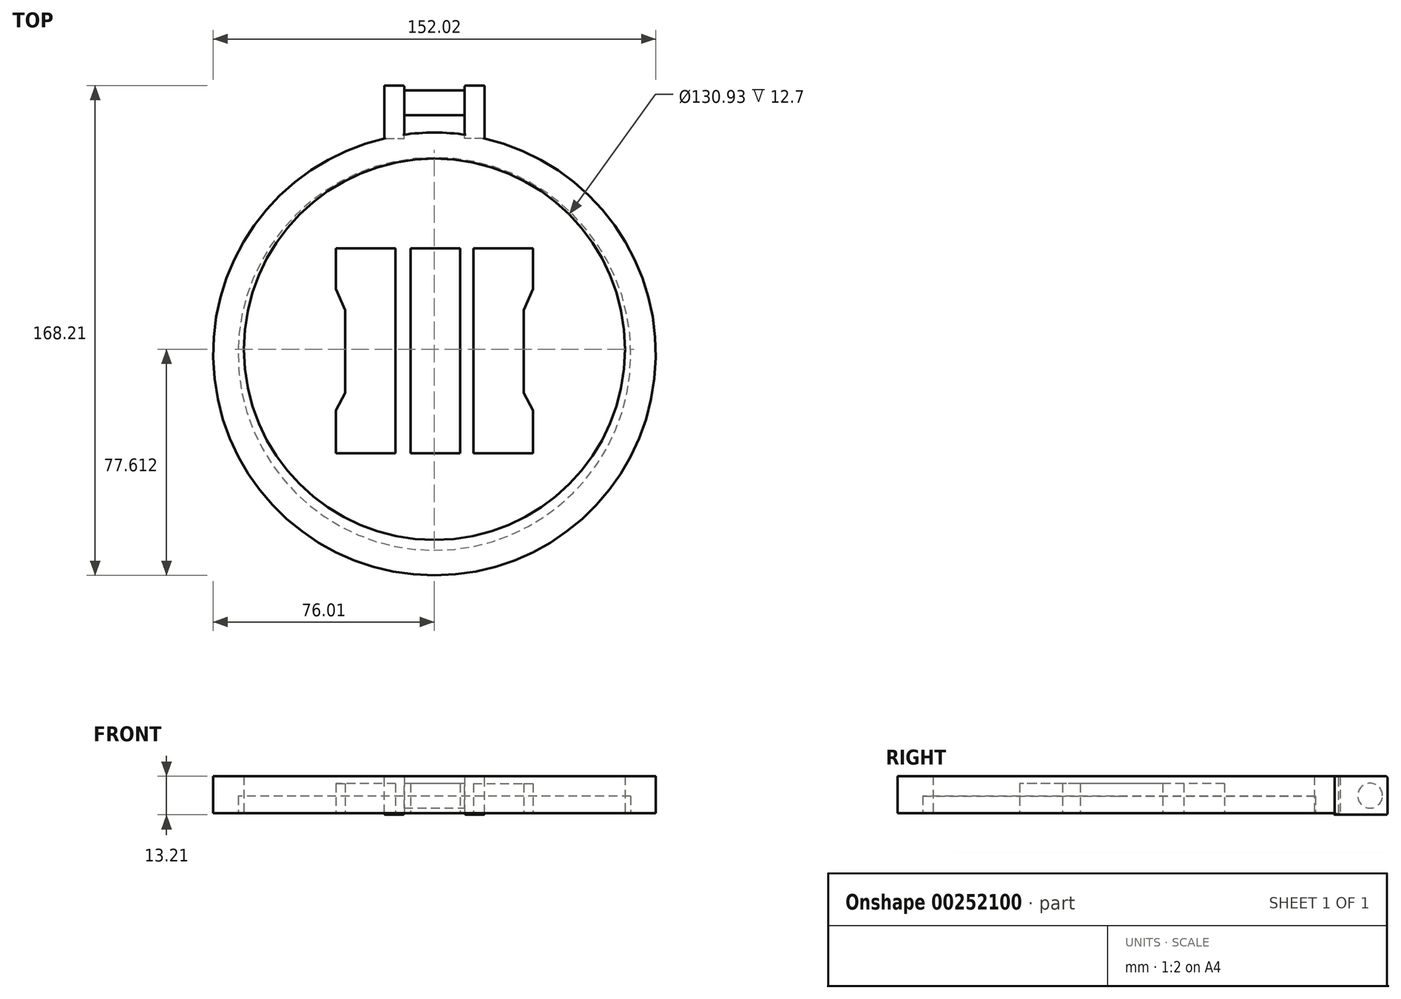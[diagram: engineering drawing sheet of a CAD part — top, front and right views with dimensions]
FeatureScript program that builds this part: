
annotation { "Feature Type Name" : "Feature", "Feature Type Description" : "" }
export const myFeature = defineFeature(function(context is Context, id is Id, definition is map)
    precondition{}
    {
        {
            var Q0;
            Q0=qCreatedBy(makeId("Top.planeOp"),FACE);
            var sketch = newSketch(context, id + "F0", { "sketchPlane" : qUnion([Q0])});
            skLineSegment(sketch, "E0", {"start": v(-13.34, 36.21) * mm, "end": v(-13.34, -34.08) * mm});
            skLineSegment(sketch, "E1", {"start": v(-13.34, 36.21) * mm, "end": v(-33.85, 36.21) * mm});
            skLineSegment(sketch, "E2", {"start": v(-33.85, 36.21) * mm, "end": v(-33.85, 22.33) * mm});
            skLineSegment(sketch, "E3", {"start": v(-33.85, 22.33) * mm, "end": v(-30.65, 15.06) * mm});
            skLineSegment(sketch, "E4", {"start": v(-30.65, 15.06) * mm, "end": v(-30.65, -13.35) * mm});
            skLineSegment(sketch, "E5", {"start": v(-30.65, -13.35) * mm, "end": v(-33.85, -19.33) * mm});
            skLineSegment(sketch, "E6", {"start": v(-33.85, -19.33) * mm, "end": v(-33.85, -34.08) * mm});
            skLineSegment(sketch, "E7", {"start": v(-33.85, -34.08) * mm, "end": v(-13.34, -34.08) * mm});
            skLineSegment(sketch, "E8", {"start": v(-8.21, 36.21) * mm, "end": v(-8.21, -34.08) * mm});
            skLineSegment(sketch, "E9", {"start": v(-8.21, -34.08) * mm, "end": v(8.88, -34.08) * mm});
            skLineSegment(sketch, "E10", {"start": v(8.88, -34.08) * mm, "end": v(8.88, 36.21) * mm});
            skLineSegment(sketch, "E11", {"start": v(8.88, 36.21) * mm, "end": v(-8.21, 36.21) * mm});
            skLineSegment(sketch, "E12.MirrorCS", {"start": v(13.34, 36.21) * mm, "end": v(33.85, 36.21) * mm});
            skLineSegment(sketch, "E13.MirrorCS", {"start": v(13.34, 36.21) * mm, "end": v(13.34, -34.08) * mm});
            skLineSegment(sketch, "E14.MirrorCS", {"start": v(33.85, 36.21) * mm, "end": v(33.85, 22.33) * mm});
            skLineSegment(sketch, "E15.MirrorCS", {"start": v(33.85, 22.33) * mm, "end": v(30.65, 15.06) * mm});
            skLineSegment(sketch, "E16.MirrorCS", {"start": v(30.65, 15.06) * mm, "end": v(30.65, -13.35) * mm});
            skLineSegment(sketch, "E17.MirrorCS", {"start": v(30.65, -13.35) * mm, "end": v(33.85, -19.33) * mm});
            skLineSegment(sketch, "E18.MirrorCS", {"start": v(33.85, -34.08) * mm, "end": v(13.34, -34.08) * mm});
            skLineSegment(sketch, "E19.MirrorCS", {"start": v(33.85, -19.33) * mm, "end": v(33.85, -34.08) * mm});
            skCircle(sketch, "E20", {"center": v(0, 0) * mm, "radius": 76.01 * mm});
            skCircle(sketch, "E21", {"center": v(0, 1.6) * mm, "radius": 65.46 * mm});
            skSolve(sketch);
        }
        {
            var Q0;
            Q0=makeQuery(id+"F0.imprint","IMPRINT",FACE,{"disambiguationData":[TD([[makeQuery(id+"F0.imprint","IMPRINT",EDGE,{"derivedFrom":sQuery(id+"F0.wireOp",EDGE,"E20")}),1.0]])]});
            extrude(context, id + "F1", {"entities" : qUnion([Q0]), "depth" : 12.7 * mm});
        }
        {
            var Q0;
            Q0=makeQuery(id+"F0.imprint","IMPRINT",FACE,{"disambiguationData":[TD([[makeQuery(id+"F0.imprint","IMPRINT",EDGE,{"derivedFrom":sQuery(id+"F0.wireOp",EDGE,"E0")}),-1.0]])]});
            var Q1;
            Q1=makeQuery(id+"F0.imprint","IMPRINT",FACE,{"disambiguationData":[TD([[makeQuery(id+"F0.imprint","IMPRINT",EDGE,{"derivedFrom":sQuery(id+"F0.wireOp",EDGE,"E8")}),1.0]])]});
            var Q2;
            Q2=makeQuery(id+"F0.imprint","IMPRINT",FACE,{"disambiguationData":[TD([[makeQuery(id+"F0.imprint","IMPRINT",EDGE,{"derivedFrom":sQuery(id+"F0.wireOp",EDGE,"E12.MirrorCS")}),-1.0]])]});
            extrude(context, id + "F2", {"entities" : qUnion([Q0, Q1, Q2]), "depth" : 10.16 * mm});
        }
        {
            var Q0;
            Q0=qCreatedBy(makeId("Top.planeOp"),FACE);
            var sketch = newSketch(context, id + "F3", { "sketchPlane" : qUnion([Q0])});
            skCircle(sketch, "E22", {"center": v(0, 0) * mm, "radius": 67.42 * mm});
            skSolve(sketch);
        }
        {
            var Q0;
            Q0 = qSketchRegion(id + "F3", true);
            extrude(context, id + "F4", {"entities" : qUnion([Q0]), "depth" : 5.84 * mm});
        }
        {
            var Q0;
            Q0=makeQuery(id+"F1.opExtrude","CAP_FACE",FACE,{"disambiguationData":[OSD([sQuery(id+"F0.wireOp",EDGE,"E20"),sQuery(id+"F0.wireOp",EDGE,"E21")])],"isStart":false});
            var sketch = newSketch(context, id + "F5", { "sketchPlane" : qUnion([Q0])});
            skLineSegment(sketch, "E23.bottom", {"start": v(-17.26, 74.03) * mm, "end": v(-10.36, 74.03) * mm});
            skLineSegment(sketch, "E23.top", {"start": v(-17.26, 92.2) * mm, "end": v(-10.36, 92.2) * mm});
            skLineSegment(sketch, "E23.left", {"start": v(-17.26, 74.03) * mm, "end": v(-17.26, 92.2) * mm});
            skLineSegment(sketch, "E23.right", {"start": v(-10.36, 74.03) * mm, "end": v(-10.36, 92.2) * mm});
            skLineSegment(sketch, "E24.MirrorCS", {"start": v(10.36, 74.03) * mm, "end": v(10.36, 92.2) * mm});
            skLineSegment(sketch, "E25.MirrorCS", {"start": v(17.26, 74.03) * mm, "end": v(10.36, 74.03) * mm});
            skLineSegment(sketch, "E26.MirrorCS", {"start": v(17.26, 74.03) * mm, "end": v(17.26, 92.2) * mm});
            skLineSegment(sketch, "E27.MirrorCS", {"start": v(17.26, 92.2) * mm, "end": v(10.36, 92.2) * mm});
            skSolve(sketch);
        }
        {
            var Q0;
            Q0 = qSketchRegion(id + "F5", true);
            extrude(context, id + "F6", {"entities" : qUnion([Q0]), "operationType" : NewBodyOperationType.ADD, "oppositeDirection" : true, "depth" : 13.2 * mm});
        }
        {
            var Q0;
            Q0=makeQuery(id+"F6.opExtrude","CAP_EDGE",EDGE,{"disambiguationData":[OSD([sQuery(id+"F5.wireOp",EDGE,"E23.top")])],"isStart":true});
            var Q1;
            Q1=makeQuery(id+"F6.opExtrude","CAP_EDGE",EDGE,{"disambiguationData":[OSD([sQuery(id+"F5.wireOp",EDGE,"E27.MirrorCS")])],"isStart":true});
            var Q2;
            Q2=makeQuery(id+"F6.opExtrude","CAP_EDGE",EDGE,{"disambiguationData":[OSD([sQuery(id+"F5.wireOp",EDGE,"E24.MirrorCS")])],"isStart":true});
            var Q3;
            Q3=makeQuery(id+"F6.opExtrude","CAP_EDGE",EDGE,{"disambiguationData":[OSD([sQuery(id+"F5.wireOp",EDGE,"E26.MirrorCS")])],"isStart":true});
            var Q4;
            Q4=makeQuery(id+"F6.opExtrude","SWEPT_EDGE",EDGE,{"disambiguationData":[OSD([sQuery(id+"F5.wireOp",EDGE,"E26.MirrorCS"),sQuery(id+"F5.wireOp",EDGE,"E27.MirrorCS")])]});
            var Q5;
            Q5=makeQuery(id+"F6.opExtrude","CAP_EDGE",EDGE,{"disambiguationData":[OSD([sQuery(id+"F5.wireOp",EDGE,"E27.MirrorCS")])],"isStart":false});
            var Q6;
            Q6=makeQuery(id+"F6.opExtrude","SWEPT_EDGE",EDGE,{"disambiguationData":[OSD([sQuery(id+"F5.wireOp",EDGE,"E24.MirrorCS"),sQuery(id+"F5.wireOp",EDGE,"E27.MirrorCS")])]});
            var Q7;
            Q7=makeQuery(id+"F6.opExtrude","SWEPT_EDGE",EDGE,{"disambiguationData":[OSD([sQuery(id+"F5.wireOp",EDGE,"E23.top"),sQuery(id+"F5.wireOp",EDGE,"E23.left")])]});
            var Q8;
            Q8=makeQuery(id+"F6.opExtrude","CAP_EDGE",EDGE,{"disambiguationData":[OSD([sQuery(id+"F5.wireOp",EDGE,"E23.top")])],"isStart":false});
            var Q9;
            Q9=makeQuery(id+"F6.opExtrude","SWEPT_EDGE",EDGE,{"disambiguationData":[OSD([sQuery(id+"F5.wireOp",EDGE,"E23.top"),sQuery(id+"F5.wireOp",EDGE,"E23.right")])]});
            var Q10;
            Q10=makeQuery(id+"F6.opExtrude","CAP_EDGE",EDGE,{"disambiguationData":[OSD([sQuery(id+"F5.wireOp",EDGE,"E24.MirrorCS")])],"isStart":false});
            var Q11;
            Q11=makeQuery(id+"F6.opExtrude","CAP_EDGE",EDGE,{"disambiguationData":[OSD([sQuery(id+"F5.wireOp",EDGE,"E23.left")])],"isStart":false});
            var Q12;
            Q12=makeQuery(id+"F6.opExtrude","CAP_EDGE",EDGE,{"disambiguationData":[OSD([sQuery(id+"F5.wireOp",EDGE,"E23.right")])],"isStart":true});
            var Q13;
            Q13=makeQuery(id+"F6.opExtrude","CAP_EDGE",EDGE,{"disambiguationData":[OSD([sQuery(id+"F5.wireOp",EDGE,"E26.MirrorCS")])],"isStart":false});
            var Q14;
            Q14=makeQuery(id+"F6.opExtrude","CAP_EDGE",EDGE,{"disambiguationData":[OSD([sQuery(id+"F5.wireOp",EDGE,"E23.left")])],"isStart":true});
            var Q15;
            Q15=makeQuery(id+"F6.opExtrude","CAP_EDGE",EDGE,{"disambiguationData":[OSD([sQuery(id+"F5.wireOp",EDGE,"E23.right")])],"isStart":false});
            fillet(context, id + "F7", {"entities" : qUnion([Q0, Q1, Q2, Q3, Q4, Q5, Q6, Q7, Q8, Q9, Q10, Q11, Q12, Q13, Q14, Q15]), "radius" : 0.5 * mm, "tangentPropagation" : true, "allowEdgeOverflow" : false});
        }
        {
            var Q0;
            Q0=makeQuery(id+"F6.opExtrude","SWEPT_FACE",FACE,{"disambiguationData":[OSD([sQuery(id+"F5.wireOp",EDGE,"E24.MirrorCS")])]});
            var sketch = newSketch(context, id + "F8", { "sketchPlane" : qUnion([Q0])});
            skCircle(sketch, "E28", {"center": v(-86.25, 6.05) * mm, "radius": 4.25 * mm});
            skSolve(sketch);
        }
        {
            var Q0;
            Q0 = qSketchRegion(id + "F8", true);
            extrude(context, id + "F9", {"entities" : qUnion([Q0]), "operationType" : NewBodyOperationType.ADD, "depth" : 25.4 * mm});
        }
    });
